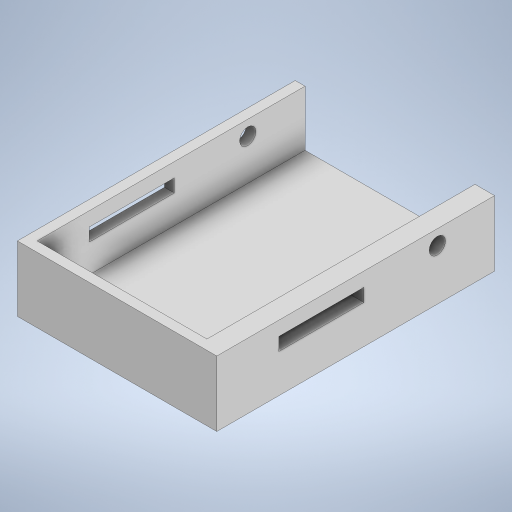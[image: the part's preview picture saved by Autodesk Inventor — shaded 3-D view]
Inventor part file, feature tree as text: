
AUTODESK INVENTOR PART (.ipt)
format: ipt  version: 2023 (Build 270158000, 158)  size: 263,680 bytes
history: native  units: in
note: dims shown in document units (in); Inventor stores cm internally (conversion verified against a paired STEP export)
features: sketch x6, extrude x5, shell x1
ambient origin geometry x8: Origin, YZ Plane, XZ Plane, XY Plane, X Axis, Y Axis, Z Axis, Center Point
bodies: Solid1 (feature_tree)
feature tree (12):
  extrude  "Extrusion1"  Depth=3.3465in
  shell  "Shell1"  Thickness=0.7874in
  sketch  "Sketch4"  dims[d4=0.1181in d17=0.3937in d18=0.0in]
  extrude  "Extrusion3"  Depth=0.3937in TaperAngle=0.0deg
  sketch  "Sketch6"  dims[d22=0.4606in d25=0.1181in d26=0.0in]
  extrude  "Extrusion5"  Depth=0.1575in
  extrude  "Extrusion6"  Depth=0.1181in TaperAngle=0.0deg
  extrude  "Extrusion8"  Depth=1.7717in
  sketch  "Sketch2"  dims[d0=2.2835in d1=3.3465in d2=0.7874in d3=0.0in]
  sketch  "Sketch5"  dims[d19=1.0236in d20=0.1575in]
  sketch  "Sketch7"  dims[d27=0.0in d28=0.0in d32=1.7717in]
  sketch  "Sketch9"  dims[d33=0.1969in d34=0.0in d35=0.0in d36=0.0787in d13=0.0197in d14=0.0344in d15=0.0197in d16=0.0344in]
